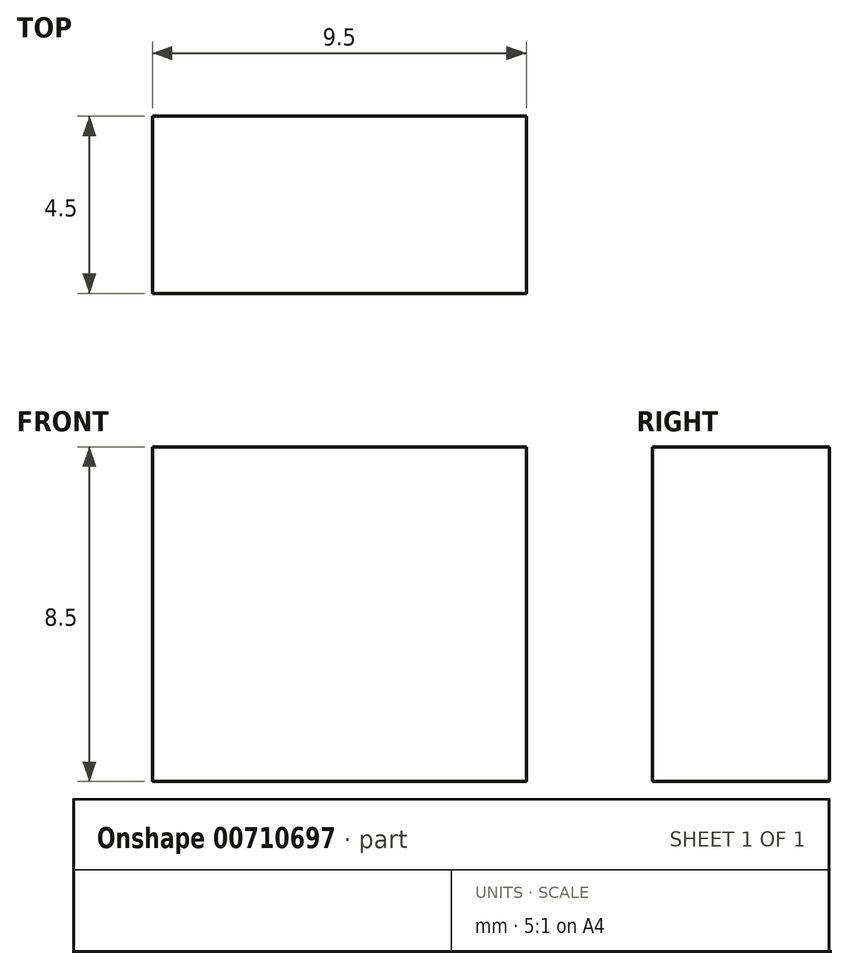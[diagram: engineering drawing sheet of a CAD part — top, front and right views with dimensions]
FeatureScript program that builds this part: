
annotation { "Feature Type Name" : "Feature", "Feature Type Description" : "" }
export const myFeature = defineFeature(function(context is Context, id is Id, definition is map)
    precondition{}
    {
        {
            var Q0;
            Q0=qCreatedBy(makeId("Top.planeOp"),FACE);
            var sketch = newSketch(context, id + "F0", { "sketchPlane" : qUnion([Q0])});
            skLineSegment(sketch, "E0.bottom", {"start": v(0, 0) * mm, "end": v(9.5, 0) * mm});
            skLineSegment(sketch, "E0.top", {"start": v(0, -4.5) * mm, "end": v(9.5, -4.5) * mm});
            skLineSegment(sketch, "E0.left", {"start": v(0, 0) * mm, "end": v(0, -4.5) * mm});
            skLineSegment(sketch, "E0.right", {"start": v(9.5, 0) * mm, "end": v(9.5, -4.5) * mm});
            skSolve(sketch);
        }
        {
            var Q0;
            Q0=makeQuery(id+"F0.imprint","IMPRINT",FACE,{"disambiguationData":[TD([[makeQuery(id+"F0.imprint","IMPRINT",EDGE,{"derivedFrom":sQuery(id+"F0.wireOp",EDGE,"E0.bottom")}),-1.0]])]});
            extrude(context, id + "F1", {"entities" : qUnion([Q0]), "depth" : 8.5 * mm, "offsetDistance" : 25 * mm});
        }
    });
